# Revit family: SH-1723
name_source: partatom
category: Lighting Fixtures
revit_build: Autodesk Revit 2017 (Build: 20160225_1515(x64)
units: mm (PartAtom-declared; Revit-internal decimal feet)

## family parameters
Cut with Voids When Loaded = No
Host = Face
Light Source = No
Part Type = Normal
Room Calculation Point = No
Round Connector Dimension = Use Diameter
Shared = No

## types (1)
- SH-1723(Black color-3000K-E27)
    Body Material = Aluminum
    Body color = Black Body
    Default Elevation = 122 cm
    Diffuser Material = Acrylic
    Height = 281 cm
    IP = IPX3
    Lamp = E27
    Manufacturer = SHOA
    Model = SH-1723
    Number of Lamps = 3
    Protection Class = Class I
    URL = https://www.shoaco.com
    Voltage/Frequency = 230v/50hz
    Wattage. = 27 W
    color temperature = 3000K
    consumption current = 0 A
    instalation = Surface mounted
    website = www.shoaco.com

## geometry (parser evidence)
native form markers: Sweep x11
no freeform markers — native parametric forms only
